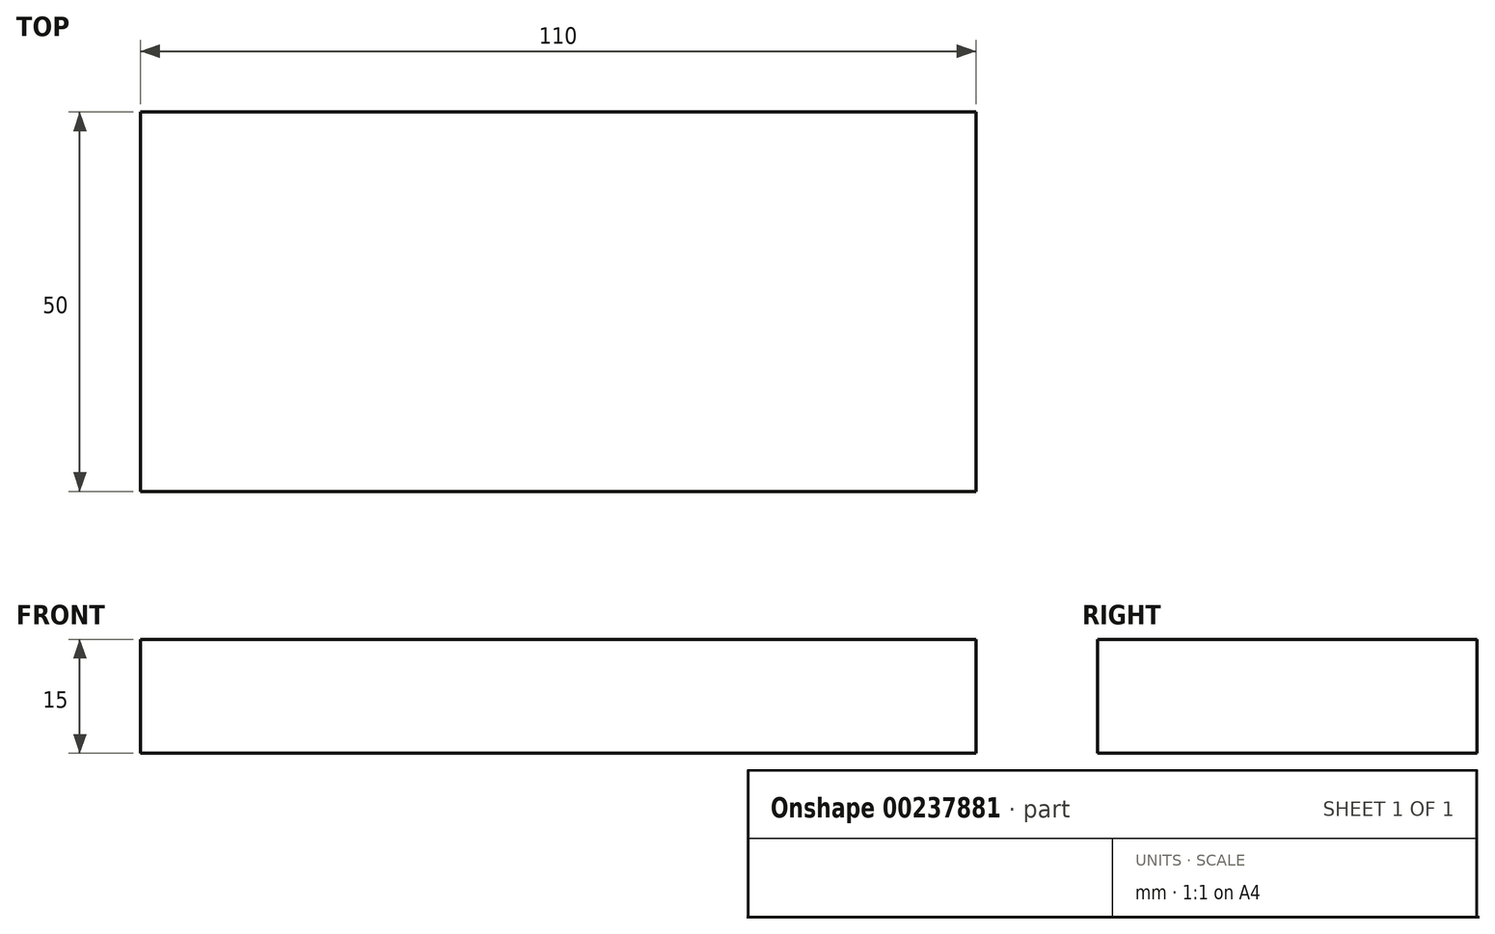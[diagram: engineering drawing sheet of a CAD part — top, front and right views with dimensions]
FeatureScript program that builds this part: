
annotation { "Feature Type Name" : "Feature", "Feature Type Description" : "" }
export const myFeature = defineFeature(function(context is Context, id is Id, definition is map)
    precondition{}
    {
        {
            var Q0;
            Q0=qCreatedBy(makeId("Top.planeOp"),FACE);
            var sketch = newSketch(context, id + "F0", { "sketchPlane" : qUnion([Q0])});
            skLineSegment(sketch, "E0.bottom", {"start": v(-55, 25) * mm, "end": v(55, 25) * mm});
            skLineSegment(sketch, "E0.top", {"start": v(-55, -25) * mm, "end": v(55, -25) * mm});
            skLineSegment(sketch, "E0.left", {"start": v(-55, 25) * mm, "end": v(-55, -25) * mm});
            skLineSegment(sketch, "E0.right", {"start": v(55, 25) * mm, "end": v(55, -25) * mm});
            skPoint(sketch, "E0.middle", {"position": v(0, 0) * mm});
            skSolve(sketch);
        }
        {
            var Q0;
            Q0 = qSketchRegion(id + "F0", true);
            extrude(context, id + "F1", {"entities" : qUnion([Q0]), "depth" : 15 * mm});
        }
    });
